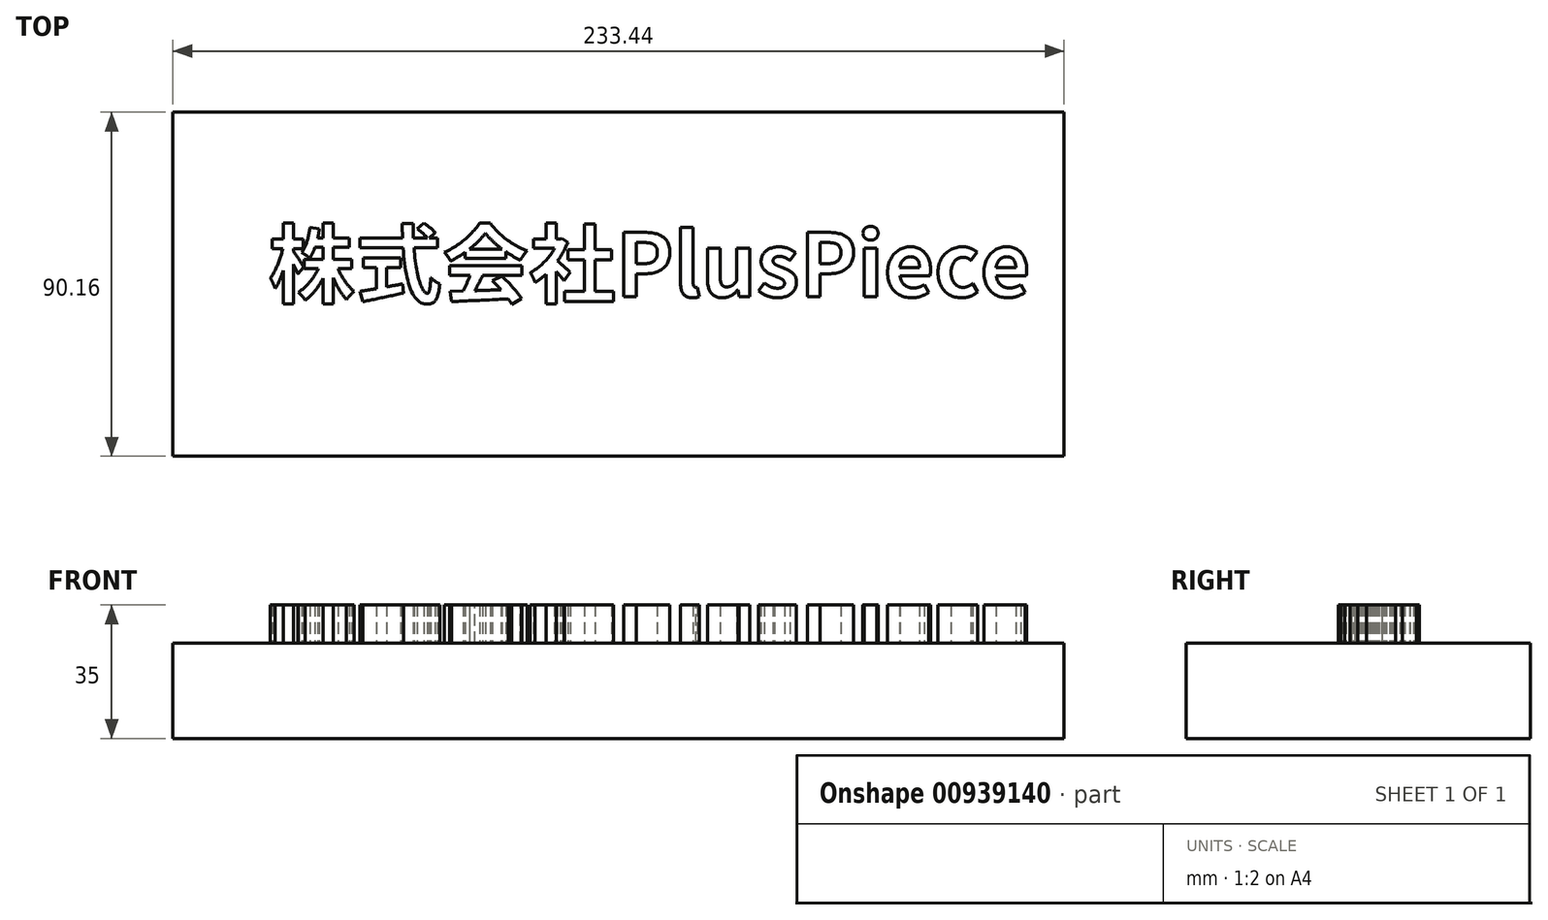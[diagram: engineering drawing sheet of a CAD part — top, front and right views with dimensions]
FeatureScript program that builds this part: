
annotation { "Feature Type Name" : "Feature", "Feature Type Description" : "" }
export const myFeature = defineFeature(function(context is Context, id is Id, definition is map)
    precondition{}
    {
        {
            var Q0;
            Q0=qCreatedBy(makeId("Top.planeOp"),FACE);
            var sketch = newSketch(context, id + "F0", { "sketchPlane" : qUnion([Q0])});
            skLineSegment(sketch, "E0.bottom", {"start": v(-108.17, 41.1) * mm, "end": v(125.27, 41.1) * mm});
            skLineSegment(sketch, "E0.top", {"start": v(-108.17, -49.07) * mm, "end": v(125.27, -49.07) * mm});
            skLineSegment(sketch, "E0.left", {"start": v(-108.17, 41.1) * mm, "end": v(-108.17, -49.07) * mm});
            skLineSegment(sketch, "E0.right", {"start": v(125.27, 41.1) * mm, "end": v(125.27, -49.07) * mm});
            skSolve(sketch);
        }
        {
            var Q0;
            Q0 = qSketchRegion(id + "F0", true);
            extrude(context, id + "F1", {"entities" : qUnion([Q0]), "depth" : 25 * mm, "offsetDistance" : 25 * mm});
        }
        {
            var Q0;
            Q0=makeQuery(id+"F1.opExtrude","CAP_FACE",FACE,{"disambiguationData":[OSD([sQuery(id+"F0.wireOp",EDGE,"E0.bottom"),sQuery(id+"F0.wireOp",EDGE,"E0.top"),sQuery(id+"F0.wireOp",EDGE,"E0.left"),sQuery(id+"F0.wireOp",EDGE,"E0.right")])],"isStart":false});
            var sketch = newSketch(context, id + "F2", { "sketchPlane" : qUnion([Q0])});
            skText(sketch, "E1", { "text": "株式会社PlusPiece", "fontName": "NotoSansCJKjp-Bold.otf"});
            const initialGuessF2  = {"E1": [-0.08317, -0.00725, 1, 0, 0.01638]};
            skSetInitialGuess(sketch, initialGuessF2);
            skSolve(sketch);
        }
        {
            var Q0;
            Q0 = qSketchRegion(id + "F2", true);
            extrude(context, id + "F3", {"entities" : qUnion([Q0]), "operationType" : NewBodyOperationType.ADD, "depth" : 10 * mm, "offsetDistance" : 25 * mm});
        }
    });
